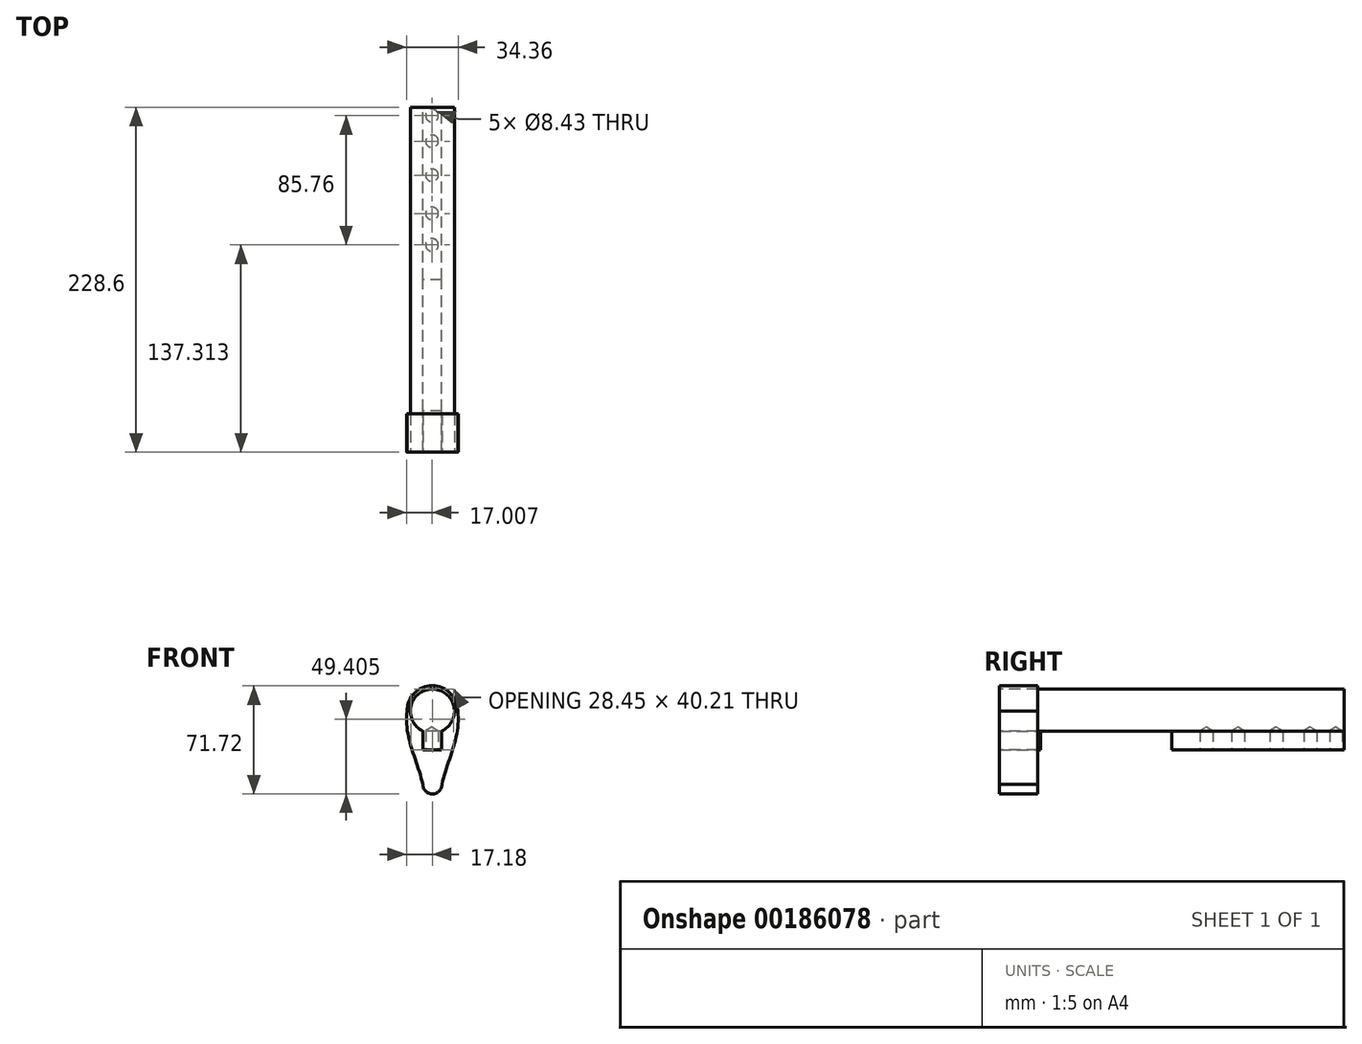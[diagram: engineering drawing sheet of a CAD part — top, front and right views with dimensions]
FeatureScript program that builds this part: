
annotation { "Feature Type Name" : "Feature", "Feature Type Description" : "" }
export const myFeature = defineFeature(function(context is Context, id is Id, definition is map)
    precondition{}
    {
        {
            var Q0;
            Q0=qCreatedBy(makeId("Front.planeOp"),FACE);
            var sketch = newSketch(context, id + "F0", { "sketchPlane" : qUnion([Q0])});
            skCircle(sketch, "E0", {"center": v(0, 16.77) * mm, "radius": 14.58 * mm});
            skLineSegment(sketch, "E1.top", {"start": v(-6.22, -8.86) * mm, "end": v(6.22, -8.86) * mm});
            skLineSegment(sketch, "E1.left", {"start": v(-6.22, 3.59) * mm, "end": v(-6.22, -8.86) * mm});
            skLineSegment(sketch, "E1.right", {"start": v(6.22, 3.59) * mm, "end": v(6.22, -8.86) * mm});
            skPoint(sketch, "E1.middle", {"position": v(0, -2.64) * mm});
            skSolve(sketch);
        }
        {
            var Q0;
            {var subQ0=sQuery(id+"F0.wireOp",EDGE,"E0");var subQ1=makeQuery(id+"F0.imprint","INTERSECT",VERTEX,{"derivedFrom":[subQ0,sQuery(id+"F0.wireOp",EDGE,"E1.left")]});Q0=makeQuery(id+"F0.imprint","IMPRINT",FACE,{"disambiguationData":[TD([[makeQuery(id+"F0.imprint","IMPRINT",EDGE,{"disambiguationData":[TD([[subQ1,-1.0]])],"derivedFrom":subQ0}),1.0]])]});}
            var Q1;
            Q1=makeQuery(id+"F0.imprint","IMPRINT",FACE,{"disambiguationData":[TD([[makeQuery(id+"F0.imprint","IMPRINT",EDGE,{"derivedFrom":sQuery(id+"F0.wireOp",EDGE,"E1.top")}),1.0]])]});
            extrude(context, id + "F1", {"entities" : qUnion([Q0, Q1]), "depth" : 228.6 * mm});
        }
        {
            var Q0;
            Q0=makeQuery(id+"F1.opExtrude","CAP_FACE",FACE,{"disambiguationData":[OSD([sQuery(id+"F0.wireOp",EDGE,"E0"),sQuery(id+"F0.wireOp",EDGE,"E1.top"),sQuery(id+"F0.wireOp",EDGE,"E1.left"),sQuery(id+"F0.wireOp",EDGE,"E1.right")])],"isStart":false});
            var sketch = newSketch(context, id + "F2", { "sketchPlane" : qUnion([Q0])});
            skCircle(sketch, "E2", {"center": v(0, 16.77) * mm, "radius": 16.79 * mm});
            skCircle(sketch, "E3", {"center": v(0, -31.81) * mm, "radius": 6.35 * mm});
            skFitSpline(sketch, "E4", {"points": [v(-16.79, 16.77) * mm, v(-6.35, -31.81) * mm], "startDerivative": vector(-7.24, -50.31) * mm, "endDerivative": vector(10.44, -48.58) * mm});
            skFitSpline(sketch, "E5.MirrorCS", {"points": [v(16.79, 16.77) * mm, v(6.35, -31.81) * mm], "startDerivative": vector(7.24, -50.31) * mm, "endDerivative": vector(-10.44, -48.58) * mm});
            skSolve(sketch);
        }
        {
            var Q0;
            {var subQ0=sQuery(id+"F2.wireOp",EDGE,"E4");Q0=makeQuery(id+"F2.imprint","IMPRINT",FACE,{"disambiguationData":[TD([[makeQuery(id+"F2.imprint","IMPRINT",EDGE,{"derivedFrom":subQ0}),1.0]])]});}
            var Q1;
            {var subQ0=sQuery(id+"F2.wireOp",EDGE,"E3");var subQ1=makeQuery(id+"F2.imprint","INTERSECT",VERTEX,{"derivedFrom":[subQ0,sQuery(id+"F2.wireOp",EDGE,"E4")]});Q1=makeQuery(id+"F2.imprint","IMPRINT",FACE,{"disambiguationData":[TD([[makeQuery(id+"F2.imprint","IMPRINT",EDGE,{"disambiguationData":[TD([[subQ1,1.0]])],"derivedFrom":subQ0}),1.0]])]});}
            var Q2;
            {var subQ0=makeQuery(id+"F1.opExtrude","CAP_EDGE",EDGE,{"disambiguationData":[OSD([sQuery(id+"F0.wireOp",EDGE,"E0")])],"isStart":false});Q2=makeQuery(id+"F2.imprint","IMPRINT",FACE,{"disambiguationData":[TD([[makeQuery(id+"F2.imprint","IMPRINT",EDGE,{"derivedFrom":subQ0}),-1.0]])]});}
            extrude(context, id + "F3", {"entities" : qUnion([Q0, Q1, Q2]), "oppositeDirection" : true, "depth" : 25.4 * mm});
        }
        {
            var Q0;
            Q0=makeQuery(id+"F1.opExtrude","SWEPT_FACE",FACE,{"disambiguationData":[OSD([sQuery(id+"F0.wireOp",EDGE,"E1.top")])]});
            var sketch = newSketch(context, id + "F4", { "sketchPlane" : qUnion([Q0])});
            skPoint(sketch, "E6", {"position": v(-0.17, 5.53) * mm});
            skPoint(sketch, "E7", {"position": v(-0.17, 22.5) * mm});
            skPoint(sketch, "E8", {"position": v(-0.17, 45.04) * mm});
            skPoint(sketch, "E9", {"position": v(-0.17, 70.37) * mm});
            skPoint(sketch, "E10", {"position": v(-0.17, 91.29) * mm});
            skSolve(sketch);
        }
        {
            var Q0;
            Q0=sQuery(id+"F4.wireOp",VERTEX,"E6");
            var Q1;
            Q1=sQuery(id+"F4.wireOp",VERTEX,"E7");
            var Q2;
            Q2=sQuery(id+"F4.wireOp",VERTEX,"E8");
            var Q3;
            Q3=sQuery(id+"F4.wireOp",VERTEX,"E9");
            var Q4;
            Q4=sQuery(id+"F4.wireOp",VERTEX,"E10");
            var Q5;
            Q5=makeQuery(id+"F1.opExtrude","SWEPT_BODY",BODY,{"disambiguationData":[OSD([sQuery(id+"F0.wireOp",EDGE,"E0"),sQuery(id+"F0.wireOp",EDGE,"E1.top"),sQuery(id+"F0.wireOp",EDGE,"E1.left"),sQuery(id+"F0.wireOp",EDGE,"E1.right")])]});
            hole(context, id + "F5", {"style" : HoleStyle.SIMPLE, "endStyle" : HoleEndStyle.BLIND, "standardTappedOrClearance" : lookupTablePath({ "standard" : "ANSI", "fit" : "Normal (ASME)", "size" : "5/16", "type" : "Clearance" }), "standardBlindInLast" : lookupTablePath({ "fit" : "Free", "standard" : "ANSI", "size" : "5/16", "type" : "Clearance" }), "holeDiameter" : 8.43 * mm, "holeDepth" : 12.7 * mm, "locations" : qUnion([Q0, Q1, Q2, Q3, Q4]), "scope" : qUnion([Q5])});
        }
        {
            var Q0;
            Q0=makeQuery(id+"F1.opExtrude","SWEPT_FACE",FACE,{"disambiguationData":[OSD([sQuery(id+"F0.wireOp",EDGE,"E1.left")])]});
            var sketch = newSketch(context, id + "F6", { "sketchPlane" : qUnion([Q0])});
            skLineSegment(sketch, "E11.bottom", {"start": v(114.3, 3.59) * mm, "end": v(201.28, 3.59) * mm});
            skLineSegment(sketch, "E11.top", {"start": v(114.3, -8.86) * mm, "end": v(201.28, -8.86) * mm});
            skLineSegment(sketch, "E11.left", {"start": v(114.3, 3.59) * mm, "end": v(114.3, -8.86) * mm});
            skLineSegment(sketch, "E11.right", {"start": v(201.28, 3.59) * mm, "end": v(201.28, -8.86) * mm});
            skSolve(sketch);
        }
        {
            var Q0;
            Q0=makeQuery(id+"F6.imprint","IMPRINT",FACE,{"disambiguationData":[TD([[makeQuery(id+"F6.imprint","IMPRINT",EDGE,{"derivedFrom":sQuery(id+"F6.wireOp",EDGE,"E11.bottom")}),1.0]])]});
            extrude(context, id + "F7", {"entities" : qUnion([Q0]), "operationType" : NewBodyOperationType.REMOVE, "endBound" : BoundingType.THROUGH_ALL, "oppositeDirection" : true, "depth" : 25.4 * mm});
        }
    });
